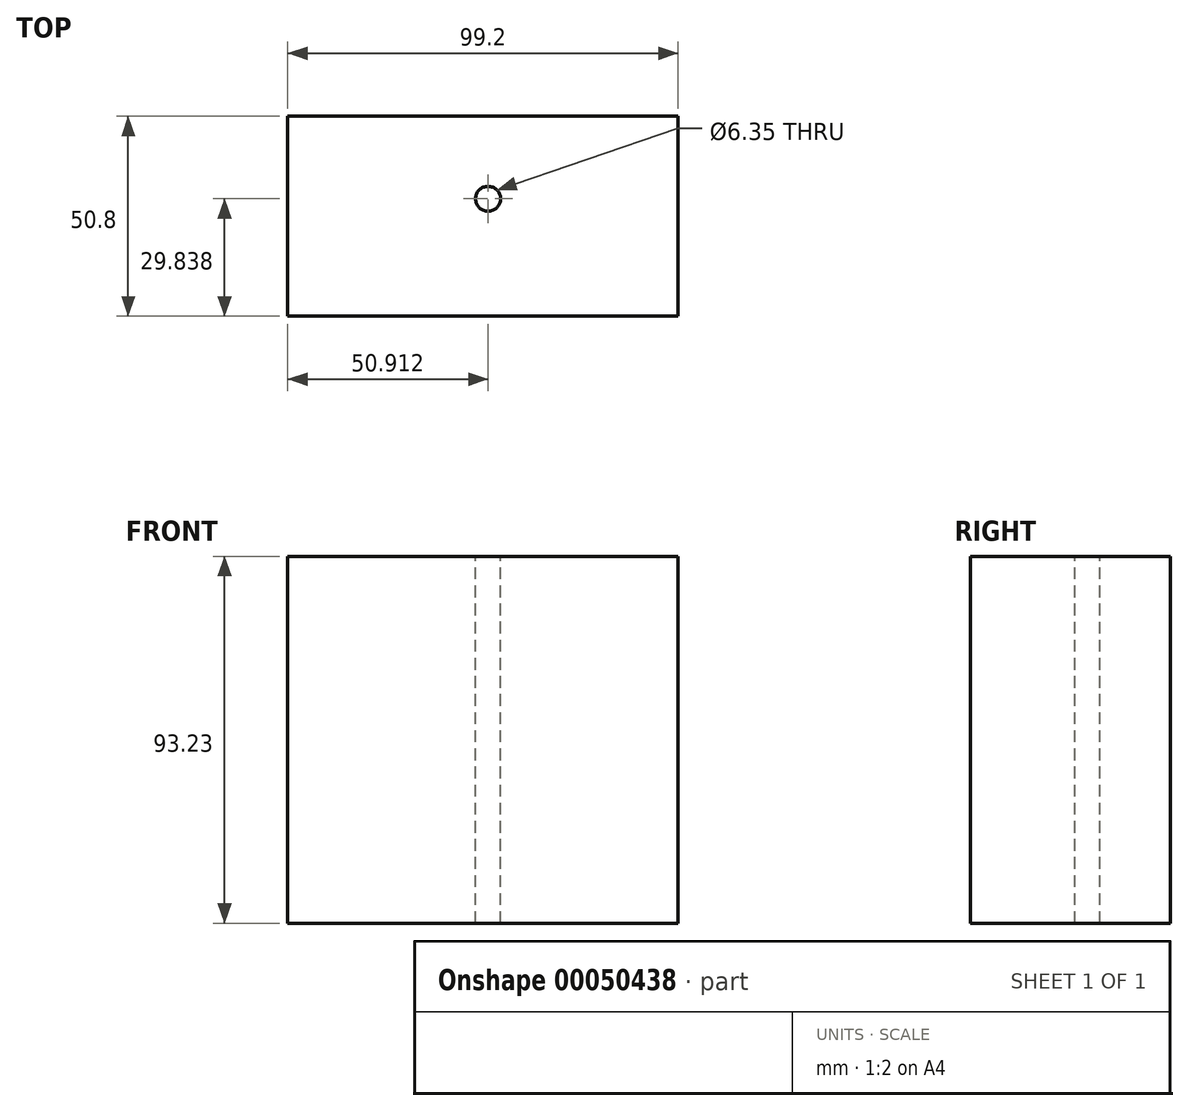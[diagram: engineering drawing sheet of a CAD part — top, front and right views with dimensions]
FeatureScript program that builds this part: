
annotation { "Feature Type Name" : "Feature", "Feature Type Description" : "" }
export const myFeature = defineFeature(function(context is Context, id is Id, definition is map)
    precondition{}
    {
        {
            var Q0;
            Q0=qCreatedBy(makeId("Front.planeOp"),FACE);
            var sketch = newSketch(context, id + "F0", { "sketchPlane" : qUnion([Q0])});
            skLineSegment(sketch, "E0.bottom", {"start": v(-46.32, 61.52) * mm, "end": v(52.88, 61.52) * mm});
            skLineSegment(sketch, "E0.top", {"start": v(-46.32, -31.7) * mm, "end": v(52.88, -31.7) * mm});
            skLineSegment(sketch, "E0.left", {"start": v(-46.32, 61.52) * mm, "end": v(-46.32, -31.7) * mm});
            skLineSegment(sketch, "E0.right", {"start": v(52.88, 61.52) * mm, "end": v(52.88, -31.7) * mm});
            skSolve(sketch);
        }
        {
            var Q0;
            Q0 = qSketchRegion(id + "F0", true);
            var Q1;
            Q1=makeQuery(id+"F0.imprint","IMPRINT",FACE,{"disambiguationData":[TD([[makeQuery(id+"F0.imprint","IMPRINT",EDGE,{"derivedFrom":sQuery(id+"F0.wireOp",EDGE,"E0.bottom")}),-1.0]])]});
            extrude(context, id + "F1", {"entities" : qUnion([Q0, Q1]), "oppositeDirection" : true, "depth" : 50.8 * mm});
        }
        {
            var Q0;
            Q0=makeQuery(id+"F1.opExtrude","SWEPT_FACE",FACE,{"disambiguationData":[OSD([sQuery(id+"F0.wireOp",EDGE,"E0.bottom")])]});
            var sketch = newSketch(context, id + "F2", { "sketchPlane" : qUnion([Q0])});
            skPoint(sketch, "E1", {"position": v(4.6, 29.84) * mm});
            skSolve(sketch);
        }
        {
            var Q0;
            Q0=sQuery(id+"F2.wireOp",VERTEX,"E1");
            var Q1;
            Q1=makeQuery(id+"F1.opExtrude","SWEPT_BODY",BODY,{"disambiguationData":[OSD([sQuery(id+"F0.wireOp",EDGE,"E0.bottom"),sQuery(id+"F0.wireOp",EDGE,"E0.top"),sQuery(id+"F0.wireOp",EDGE,"E0.left"),sQuery(id+"F0.wireOp",EDGE,"E0.right")])]});
            hole(context, id + "F3", {"style" : HoleStyle.SIMPLE, "holeDiameter" : 6.35 * mm, "endStyle" : HoleEndStyle.THROUGH, "locations" : qUnion([Q0]), "scope" : qUnion([Q1])});
        }
    });
